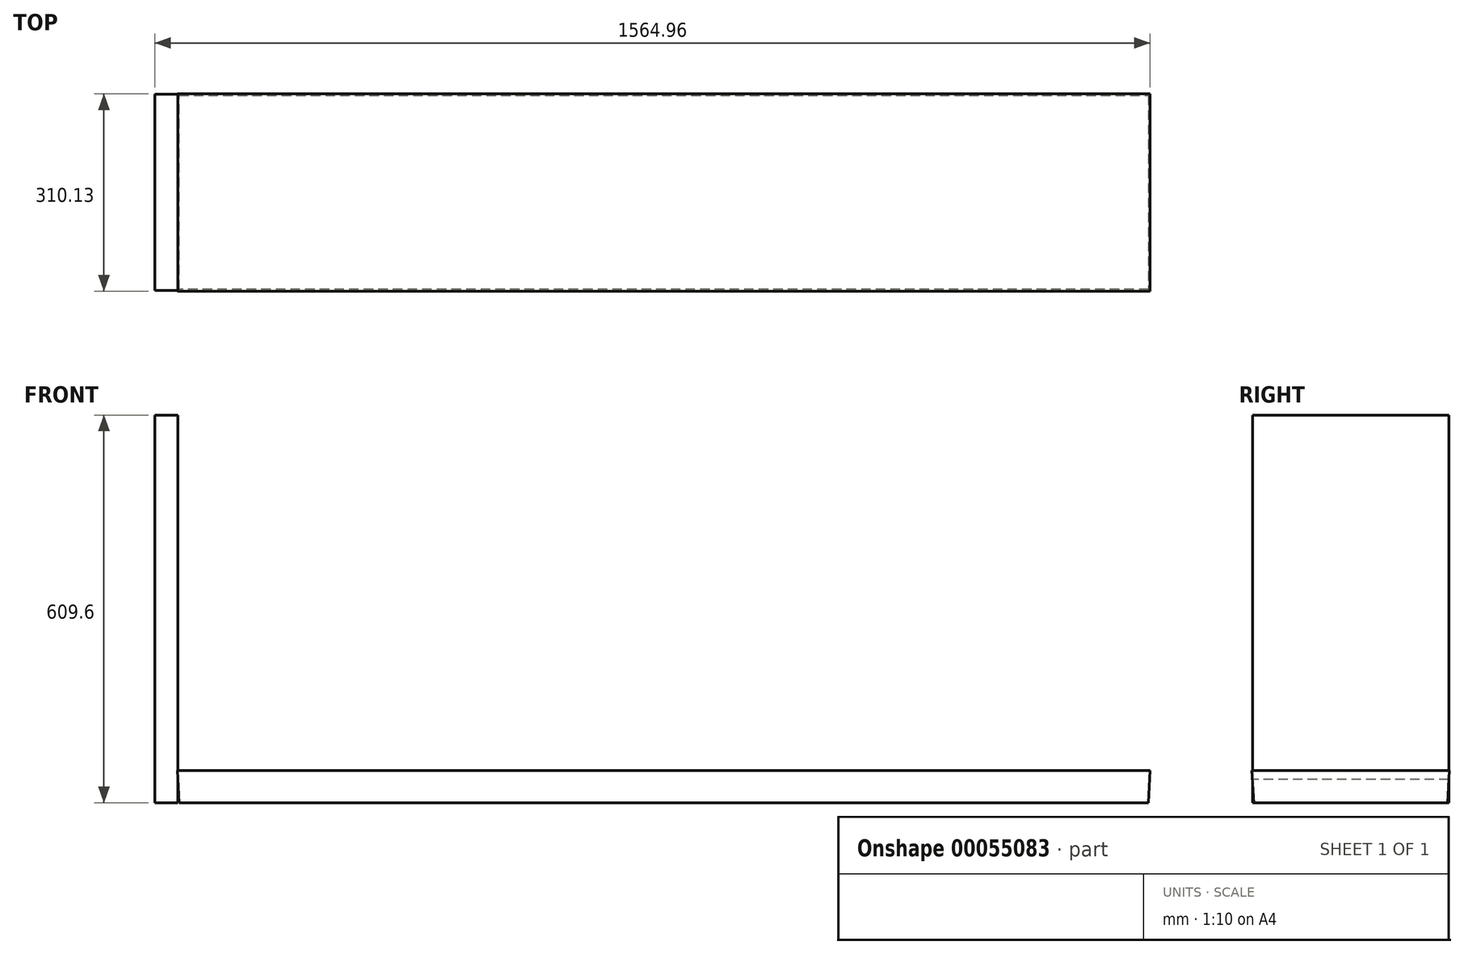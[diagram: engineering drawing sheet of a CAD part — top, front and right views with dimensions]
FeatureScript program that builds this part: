
annotation { "Feature Type Name" : "Feature", "Feature Type Description" : "" }
export const myFeature = defineFeature(function(context is Context, id is Id, definition is map)
    precondition{}
    {
        {
            var Q0;
            Q0=qCreatedBy(makeId("Top.planeOp"),FACE);
            var sketch = newSketch(context, id + "F0", { "sketchPlane" : qUnion([Q0])});
            skLineSegment(sketch, "E0.bottom", {"start": v(-763.66, 73.38) * mm, "end": v(760.34, 73.38) * mm});
            skLineSegment(sketch, "E0.top", {"start": v(-763.66, -231.42) * mm, "end": v(760.34, -231.42) * mm});
            skLineSegment(sketch, "E0.left", {"start": v(-763.66, 73.38) * mm, "end": v(-763.66, -231.42) * mm});
            skLineSegment(sketch, "E0.right", {"start": v(760.34, 73.38) * mm, "end": v(760.34, -231.42) * mm});
            skSolve(sketch);
        }
        {
            var Q0;
            Q0 = qSketchRegion(id + "FOvcesnIRRsJzqQ_0", true);
            var Q1;
            Q1=makeQuery(id+"F0.imprint","IMPRINT",FACE,{"disambiguationData":[TD([[makeQuery(id+"F0.imprint","IMPRINT",EDGE,{"derivedFrom":sQuery(id+"F0.wireOp",EDGE,"E0.bottom")}),-1.0]])]});
            extrude(context, id + "F1", {"entities" : qUnion([Q0, Q1]), "depth" : 25.4 * mm, "hasDraft" : true, "draftAngle" : 3 * degree});
        }
        {
            var Q0;
            Q0 = qSketchRegion(id + "F0", true);
            var sketch = newSketch(context, id + "F2", { "sketchPlane" : qUnion([Q0])});
            skSolve(sketch);
        }
        {
            var Q0;
            Q0 = qSketchRegion(id + "F2", true);
            var Q1;
            Q1=makeQuery(id+"F1.opExtrude","CAP_FACE",FACE,{"disambiguationData":[OSD([sQuery(id+"F0.wireOp",EDGE,"E0.bottom"),sQuery(id+"F0.wireOp",EDGE,"E0.top"),sQuery(id+"F0.wireOp",EDGE,"E0.left"),sQuery(id+"F0.wireOp",EDGE,"E0.right")])],"isStart":false});
            extrude(context, id + "F3", {"entities" : qUnion([Q0, Q1]), "operationType" : NewBodyOperationType.ADD, "depth" : 25.4 * mm, "hasDraft" : true, "draftAngle" : 3 * degree});
        }
        {
            var Q0;
            Q0=qCreatedBy(makeId("Top.planeOp"),FACE);
            var sketch = newSketch(context, id + "F4", { "sketchPlane" : qUnion([Q0])});
            skLineSegment(sketch, "E1.bottom", {"start": v(-801.96, 75.64) * mm, "end": v(-765.58, 75.64) * mm});
            skLineSegment(sketch, "E1.top", {"start": v(-801.96, -233.05) * mm, "end": v(-765.58, -233.05) * mm});
            skLineSegment(sketch, "E1.left", {"start": v(-801.96, 75.64) * mm, "end": v(-801.96, -233.05) * mm});
            skLineSegment(sketch, "E1.right", {"start": v(-765.58, 75.64) * mm, "end": v(-765.58, -233.05) * mm});
            skSolve(sketch);
        }
        {
            var Q0;
            Q0=makeQuery(id+"F4.imprint","IMPRINT",FACE,{"disambiguationData":[TD([[makeQuery(id+"F4.imprint","IMPRINT",EDGE,{"derivedFrom":sQuery(id+"F4.wireOp",EDGE,"E1.bottom")}),-1.0]])]});
            extrude(context, id + "F5", {"entities" : qUnion([Q0]), "operationType" : NewBodyOperationType.ADD, "depth" : 609.6 * mm, "offsetDistance" : 25.4 * mm});
        }
    });
